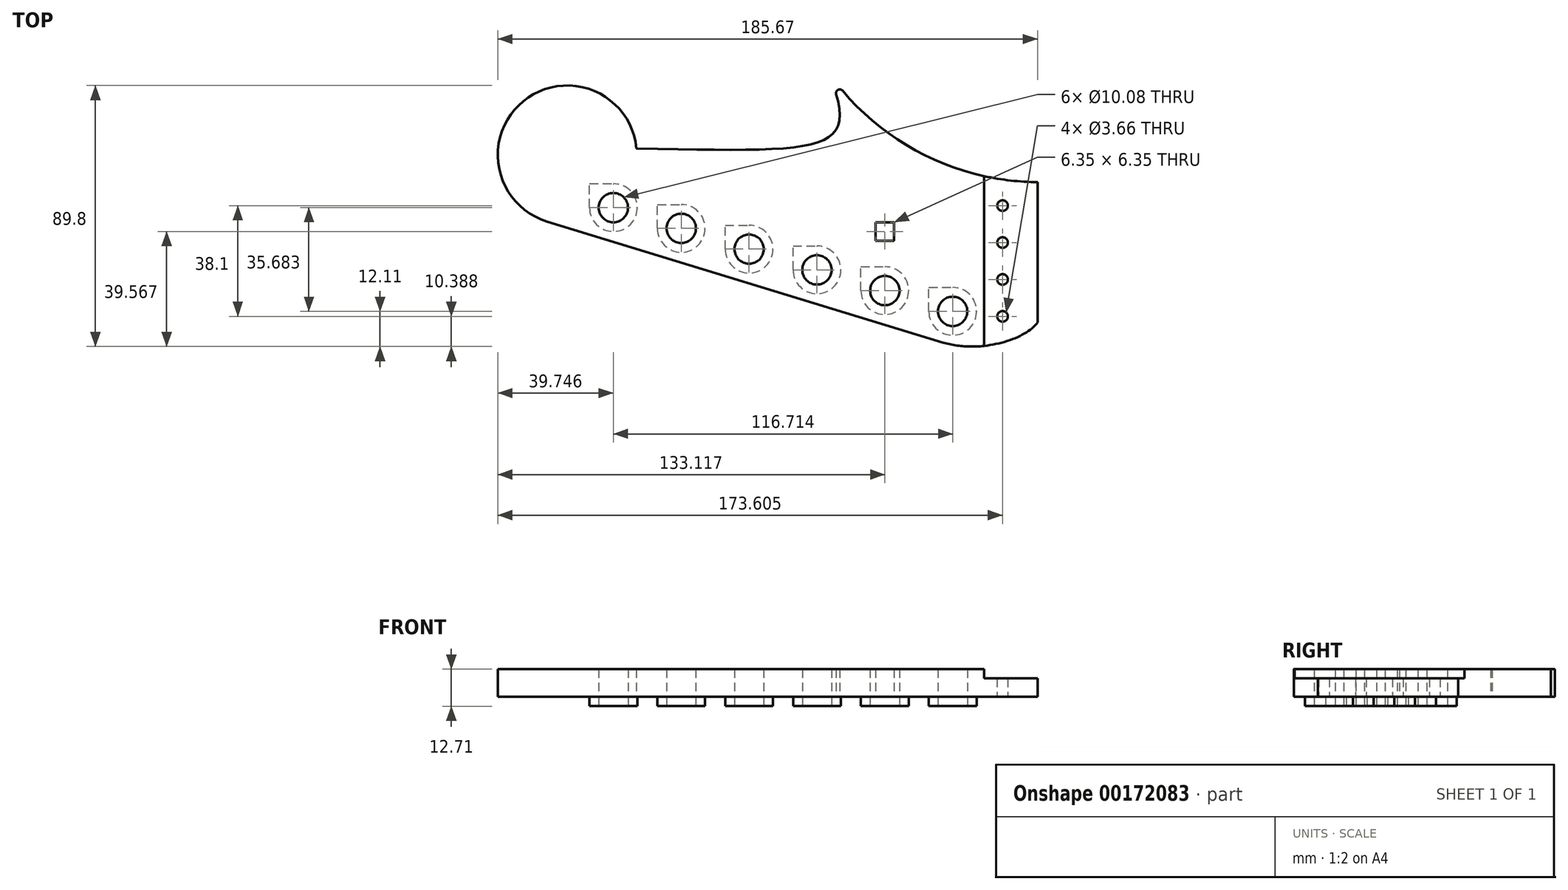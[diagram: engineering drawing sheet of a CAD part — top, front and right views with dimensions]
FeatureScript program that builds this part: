
annotation { "Feature Type Name" : "Feature", "Feature Type Description" : "" }
export const myFeature = defineFeature(function(context is Context, id is Id, definition is map)
    precondition{}
    {
        {
            var Q0;
            Q0=qCreatedBy(makeId("Top.planeOp"),FACE);
            var sketch = newSketch(context, id + "F0", { "sketchPlane" : qUnion([Q0])});
            skPoint(sketch, "E0", {"position": v(-185.67, 33.46) * mm});
            skLineSegment(sketch, "E1", {"start": v(0, 24.13) * mm, "end": v(0, -24.13) * mm});
            skCircle(sketch, "E2", {"center": v(-29.21, -20.32) * mm, "radius": 5.04 * mm});
            skLineSegment(sketch, "E3", {"start": v(0, 0) * mm, "end": v(0, 0) * mm});
            skPoint(sketch, "E3.endSnap0", {"position": v(0, 0) * mm});
            skCircle(sketch, "E4.1.0.0", {"center": v(-52.55, -13.18) * mm, "radius": 5.04 * mm});
            skCircle(sketch, "E4.2.0.0", {"center": v(-75.9, -6.05) * mm, "radius": 5.04 * mm});
            skCircle(sketch, "E4.3.0.0", {"center": v(-99.24, 1.09) * mm, "radius": 5.04 * mm});
            skCircle(sketch, "E4.4.0.0", {"center": v(-122.58, 8.23) * mm, "radius": 5.04 * mm});
            skCircle(sketch, "E4.5.0.0", {"center": v(-145.92, 15.36) * mm, "radius": 5.04 * mm});
            skLineSegment(sketch, "E4.direction1", {"start": v(-29.21, -20.32) * mm, "end": v(-52.55, -13.18) * mm, "construction": true});
            skLineSegment(sketch, "E5", {"start": v(-18.42, 26.22) * mm, "end": v(-18.41, -32.2) * mm});
            skLineSegment(sketch, "E6", {"start": v(-32.5, -31.06) * mm, "end": v(-168.76, 10.6) * mm});
            skLineSegment(sketch, "E7", {"start": v(-29.21, -20.32) * mm, "end": v(-32.5, -31.06) * mm, "construction": true});
            skFitSpline(sketch, "E8", {"points": [v(-32.5, -31.06) * mm, v(0, -24.13) * mm], "startDerivative": vector(36.44, -11.14) * mm, "endDerivative": vector(14.29, 19.05) * mm});
            skLineSegment(sketch, "E9", {"start": v(0, 0) * mm, "end": v(99.12, 0) * mm, "construction": true});
            skArc(sketch, "E10", {"start": v(-168.76, 10.6) * mm, "mid": v(-180.99, 19.25) * mm, "end": v(-185.67, 33.46) * mm});
            skLineSegment(sketch, "E11", {"start": v(-185.67, 33.46) * mm, "end": v(-185.67, 61.73) * mm, "construction": true});
            skArc(sketch, "E12", {"start": v(-137.98, 35.75) * mm, "mid": v(-162.91, 57.34) * mm, "end": v(-185.67, 33.46) * mm});
            skArc(sketch, "E13", {"start": v(-72.27, 62.33) * mm, "mid": v(-40.79, 34.43) * mm, "end": v(0, 24.13) * mm});
            skLineSegment(sketch, "E14", {"start": v(8.57, 3.57) * mm, "end": v(-99.24, 3.57) * mm, "construction": true});
            skLineSegment(sketch, "E15", {"start": v(8.57, -3.57) * mm, "end": v(-75.9, -3.57) * mm, "construction": true});
            skCircle(sketch, "E16", {"center": v(-75.9, -6.05) * mm, "radius": 2.48 * mm});
            skCircle(sketch, "E17", {"center": v(-99.24, 1.09) * mm, "radius": 2.48 * mm});
            skLineSegment(sketch, "E18", {"start": v(-99.24, 3.57) * mm, "end": v(-99.24, 1.09) * mm, "construction": true});
            skLineSegment(sketch, "E19", {"start": v(-75.9, -3.57) * mm, "end": v(-75.9, -6.05) * mm, "construction": true});
            skLineSegment(sketch, "E20", {"start": v(-137.98, 35.75) * mm, "end": v(-72.27, 62.33) * mm, "construction": true});
            skFitSpline(sketch, "E21", {"points": [v(-137.98, 35.75) * mm, v(-72.27, 62.33) * mm], "startDerivative": vector(194.61, -3.65) * mm, "endDerivative": vector(-37.72, 87.36) * mm});
            skCircle(sketch, "E22", {"center": v(-122.58, 8.23) * mm, "radius": 2.48 * mm});
            skCircle(sketch, "E23", {"center": v(-145.92, 15.36) * mm, "radius": 2.48 * mm});
            skLineSegment(sketch, "E24", {"start": v(-122.58, 8.23) * mm, "end": v(-122.58, 10.7) * mm});
            skLineSegment(sketch, "E25", {"start": v(-145.92, 15.36) * mm, "end": v(-145.92, 17.84) * mm});
            skLineSegment(sketch, "E26", {"start": v(-122.58, 10.7) * mm, "end": v(7.67, 10.7) * mm, "construction": true});
            skLineSegment(sketch, "E27", {"start": v(-145.92, 17.84) * mm, "end": v(21.7, 17.84) * mm, "construction": true});
            skSolve(sketch);
        }
        {
            var Q0;
            Q0=qSketchRegion(id+"F0",true);
            extrude(context, id + "F1", {"entities" : qUnion([Q0]), "depth" : 6.35 * mm});
        }
        {
            var Q0;
            Q0=makeQuery(id+"F0.imprint","IMPRINT",FACE,{"disambiguationData":[TD([[makeQuery(id+"F0.imprint","IMPRINT",EDGE,{"derivedFrom":sQuery(id+"F0.wireOp",EDGE,"E2")}),-1.0]])]});
            extrude(context, id + "F2", {"entities" : qUnion([Q0]), "operationType" : NewBodyOperationType.ADD, "depth" : 9.52 * mm});
        }
        {
            var Q0;
            Q0=makeQuery(id+"F1.opExtrude","CAP_FACE",FACE,{"disambiguationData":[OSD([sQuery(id+"F0.wireOp",EDGE,"4aa001a9-7916-4ac9-b611-f33505b9f3c5"),sQuery(id+"F0.wireOp",EDGE,"77602153-f705-4483-a7fc-31cc86b3ea61"),sQuery(id+"F0.wireOp",EDGE,"ee52411e-a9e7-4ef9-bd5f-1803b2297118"),sQuery(id+"F0.wireOp",EDGE,"E1"),sQuery(id+"F0.wireOp",EDGE,"E2"),sQuery(id+"F0.wireOp",EDGE,"E4.1.0.0"),sQuery(id+"F0.wireOp",EDGE,"E4.2.0.0"),sQuery(id+"F0.wireOp",EDGE,"E4.3.0.0"),sQuery(id+"F0.wireOp",EDGE,"E4.4.0.0"),sQuery(id+"F0.wireOp",EDGE,"E4.5.0.0"),sQuery(id+"F0.wireOp",EDGE,"05dfdfb5-9140-4733-bf36-b7656169c247"),sQuery(id+"F0.wireOp",EDGE,"fa98ec53-b239-455b-819f-4d27d42f24a3")])],"isStart":false});
            var sketch = newSketch(context, id + "F3", { "sketchPlane" : qUnion([Q0])});
            skPoint(sketch, "E28", {"position": v(-12.06, -22.04) * mm});
            skPoint(sketch, "E29", {"position": v(-12.06, 16.06) * mm});
            skPoint(sketch, "E30", {"position": v(-12.07, 3.36) * mm});
            skPoint(sketch, "E31", {"position": v(-12.06, -9.34) * mm});
            skLineSegment(sketch, "E32", {"start": v(0, -3) * mm, "end": v(-18.41, -3) * mm, "construction": true});
            skSolve(sketch);
        }
        {
            var Q0;
            Q0=sQuery(id+"F3.wireOp",VERTEX,"E29");
            var Q1;
            Q1=sQuery(id+"F3.wireOp",VERTEX,"E30");
            var Q2;
            Q2=sQuery(id+"F3.wireOp",VERTEX,"E31");
            var Q3;
            Q3=sQuery(id+"F3.wireOp",VERTEX,"E28");
            var Q4;
            Q4=makeQuery(id+"F1.opExtrude","SWEPT_BODY",BODY,{"disambiguationData":[OSD([sQuery(id+"F0.wireOp",EDGE,"4aa001a9-7916-4ac9-b611-f33505b9f3c5"),sQuery(id+"F0.wireOp",EDGE,"77602153-f705-4483-a7fc-31cc86b3ea61"),sQuery(id+"F0.wireOp",EDGE,"ee52411e-a9e7-4ef9-bd5f-1803b2297118"),sQuery(id+"F0.wireOp",EDGE,"E1"),sQuery(id+"F0.wireOp",EDGE,"E2"),sQuery(id+"F0.wireOp",EDGE,"E4.1.0.0"),sQuery(id+"F0.wireOp",EDGE,"E4.2.0.0"),sQuery(id+"F0.wireOp",EDGE,"E4.3.0.0"),sQuery(id+"F0.wireOp",EDGE,"E4.4.0.0"),sQuery(id+"F0.wireOp",EDGE,"E4.5.0.0"),sQuery(id+"F0.wireOp",EDGE,"05dfdfb5-9140-4733-bf36-b7656169c247"),sQuery(id+"F0.wireOp",EDGE,"fa98ec53-b239-455b-819f-4d27d42f24a3")])]});
            hole(context, id + "F4", {"style" : HoleStyle.SIMPLE, "endStyle" : HoleEndStyle.THROUGH, "standardTappedOrClearance" : lookupTablePath({ "standard" : "ANSI", "fit" : "Close", "size" : "#6", "type" : "Clearance" }), "standardBlindInLast" : lookupTablePath({ "fit" : "Close", "standard" : "ANSI", "size" : "#6", "type" : "Clearance" }), "holeDiameter" : 3.66 * mm, "locations" : qUnion([Q0, Q1, Q2, Q3]), "scope" : qUnion([Q4]), "isTappedThrough" : true, "startStyle" : HoleStartStyle.SKETCH});
        }
        {
            var Q0;
            {var subQ0=sQuery(id+"F0.wireOp",EDGE,"E21");var subQ1=sQuery(id+"F0.wireOp",EDGE,"E13");Q0=makeQuery(id+"F2.boolean.opBoolean","MERGE",EDGE,{"derivedFrom":[makeQuery(id+"F1.opExtrude","SWEPT_EDGE",EDGE,{"disambiguationData":[OSD([subQ1,subQ0])]}),makeQuery(id+"F2.opExtrude","SWEPT_EDGE",EDGE,{"disambiguationData":[OSD([subQ1,subQ0])]})]});}
            fillet(context, id + "F5", {"entities" : qUnion([Q0]), "radius" : 1.27 * mm, "tangentPropagation" : true, "allowEdgeOverflow" : false});
        }
        {
            var Q0;
            Q0=makeQuery(id+"F2.opExtrude","CAP_FACE",FACE,{"disambiguationData":[OSD([sQuery(id+"F0.wireOp",EDGE,"E2"),sQuery(id+"F0.wireOp",EDGE,"E4.1.0.0"),sQuery(id+"F0.wireOp",EDGE,"E4.2.0.0"),sQuery(id+"F0.wireOp",EDGE,"E4.3.0.0"),sQuery(id+"F0.wireOp",EDGE,"E4.4.0.0"),sQuery(id+"F0.wireOp",EDGE,"E4.5.0.0"),sQuery(id+"F0.wireOp",EDGE,"E5"),sQuery(id+"F0.wireOp",EDGE,"E6"),sQuery(id+"F0.wireOp",EDGE,"E8"),sQuery(id+"F0.wireOp",EDGE,"E10"),sQuery(id+"F0.wireOp",EDGE,"E12"),sQuery(id+"F0.wireOp",EDGE,"E13"),sQuery(id+"F0.wireOp",EDGE,"E21")])],"isStart":false});
            var sketch = newSketch(context, id + "F6", { "sketchPlane" : qUnion([Q0])});
            skArc(sketch, "E33", {"start": v(-176.02, 0) * mm, "mid": v(-95.34, 4.1) * mm, "end": v(-40.97, 63.86) * mm});
            skArc(sketch, "E34.0", {"start": v(-172.8, 9.1) * mm, "mid": v(-99.46, 12.82) * mm, "end": v(-50.05, 67.14) * mm});
            skArc(sketch, "E35", {"start": v(-33.84, 84.78) * mm, "mid": v(-42.65, 23.63) * mm, "end": v(-29.69, -36.76) * mm});
            skArc(sketch, "E36.0", {"start": v(-38.9, 86.46) * mm, "mid": v(-47.98, 23.45) * mm, "end": v(-34.62, -38.79) * mm});
            skArc(sketch, "E37", {"start": v(-118.56, -20.84) * mm, "mid": v(-145.78, 28.3) * mm, "end": v(-199.55, 44.5) * mm});
            skArc(sketch, "E38.0", {"start": v(-108.22, -19.6) * mm, "mid": v(-139.24, 36.4) * mm, "end": v(-200.52, 54.87) * mm});
            skLineSegment(sketch, "E39.0", {"start": v(-32.5, -31.06) * mm, "end": v(-168.76, 10.6) * mm});
            skArc(sketch, "E39.1", {"start": v(-137.98, 35.75) * mm, "mid": v(-176.9, 51.98) * mm, "end": v(-168.76, 10.6) * mm});
            skFitSpline(sketch, "E39.2", {"points": [v(-137.98, 35.75) * mm, v(-73.1, 34.53) * mm, v(-60.64, 33.21) * mm, v(-73.21, 62.33) * mm]});
            skArc(sketch, "E39.3", {"start": v(-67.1, 55.59) * mm, "mid": v(-68.68, 55.88) * mm, "end": v(-69.28, 54.4) * mm});
            skArc(sketch, "E39.4", {"start": v(-67.1, 55.59) * mm, "mid": v(-45.17, 36.9) * mm, "end": v(-18.41, 26.22) * mm});
            skFitSpline(sketch, "E39.5", {"points": [v(-32.5, -31.06) * mm, v(-20.35, -34.77) * mm, v(-4.76, -30.48) * mm, v(0, -24.13) * mm]});
            skLineSegment(sketch, "E39.6", {"start": v(-18.42, 26.22) * mm, "end": v(-18.41, -32.2) * mm});
            skSolve(sketch);
        }
        {
            var Q0;
            Q0=makeQuery(id+"F2.opExtrude","CAP_FACE",FACE,{"disambiguationData":[OSD([sQuery(id+"F0.wireOp",EDGE,"E2"),sQuery(id+"F0.wireOp",EDGE,"E4.1.0.0"),sQuery(id+"F0.wireOp",EDGE,"E4.2.0.0"),sQuery(id+"F0.wireOp",EDGE,"E4.3.0.0"),sQuery(id+"F0.wireOp",EDGE,"E4.4.0.0"),sQuery(id+"F0.wireOp",EDGE,"E4.5.0.0"),sQuery(id+"F0.wireOp",EDGE,"E5"),sQuery(id+"F0.wireOp",EDGE,"E6"),sQuery(id+"F0.wireOp",EDGE,"E8"),sQuery(id+"F0.wireOp",EDGE,"E10"),sQuery(id+"F0.wireOp",EDGE,"E12"),sQuery(id+"F0.wireOp",EDGE,"E13"),sQuery(id+"F0.wireOp",EDGE,"E21")])],"isStart":false});
            var sketch = newSketch(context, id + "F7", { "sketchPlane" : qUnion([Q0])});
            skLineSegment(sketch, "E40", {"start": v(-13.49, 50.46) * mm, "end": v(-120.4, -45.77) * mm});
            skLineSegment(sketch, "E41", {"start": v(-120.4, -45.77) * mm, "end": v(-124.32, -41.42) * mm});
            skLineSegment(sketch, "E42", {"start": v(-124.32, -41.42) * mm, "end": v(-17.2, 55) * mm});
            skLineSegment(sketch, "E43", {"start": v(-17.2, 55) * mm, "end": v(-13.49, 50.46) * mm});
            skLineSegment(sketch, "E44", {"start": v(-49.09, -54.74) * mm, "end": v(-69.94, 75.3) * mm});
            skLineSegment(sketch, "E45", {"start": v(-69.94, 75.3) * mm, "end": v(-75.5, 74.4) * mm});
            skLineSegment(sketch, "E46", {"start": v(-75.5, 74.4) * mm, "end": v(-54.41, -57.09) * mm});
            skLineSegment(sketch, "E47", {"start": v(-54.41, -57.09) * mm, "end": v(-49.09, -54.74) * mm});
            skLineSegment(sketch, "E48", {"start": v(-151.73, -17.56) * mm, "end": v(37.22, 6.84) * mm});
            skLineSegment(sketch, "E49", {"start": v(37.22, 6.84) * mm, "end": v(35.94, 14.83) * mm});
            skLineSegment(sketch, "E50", {"start": v(35.94, 14.83) * mm, "end": v(-152.1, -9.45) * mm});
            skLineSegment(sketch, "E51", {"start": v(-152.1, -9.45) * mm, "end": v(-151.73, -17.56) * mm});
            skLineSegment(sketch, "E52", {"start": v(-167.26, 91.8) * mm, "end": v(-135.04, -31.2) * mm});
            skLineSegment(sketch, "E53", {"start": v(-135.04, -31.2) * mm, "end": v(-143.78, -33.49) * mm});
            skLineSegment(sketch, "E54", {"start": v(-143.78, -33.49) * mm, "end": v(-175.54, 87.77) * mm});
            skLineSegment(sketch, "E55", {"start": v(-175.54, 87.77) * mm, "end": v(-167.26, 91.8) * mm});
            skLineSegment(sketch, "E56", {"start": v(-107.47, 85.6) * mm, "end": v(-120.17, 6.32) * mm});
            skLineSegment(sketch, "E57", {"start": v(-120.17, 6.32) * mm, "end": v(-125.36, 7.15) * mm});
            skLineSegment(sketch, "E58", {"start": v(-125.36, 7.15) * mm, "end": v(-112.55, 87.16) * mm});
            skLineSegment(sketch, "E59", {"start": v(-112.55, 87.16) * mm, "end": v(-107.47, 85.6) * mm});
            skLineSegment(sketch, "E60", {"start": v(-28.5, -37.42) * mm, "end": v(-138.14, 44.12) * mm});
            skLineSegment(sketch, "E61", {"start": v(-138.14, 44.12) * mm, "end": v(-135.1, 48.2) * mm});
            skLineSegment(sketch, "E62", {"start": v(-135.1, 48.2) * mm, "end": v(-25, -33.69) * mm});
            skLineSegment(sketch, "E63", {"start": v(-25, -33.69) * mm, "end": v(-28.5, -37.42) * mm});
            skLineSegment(sketch, "E64", {"start": v(-38.7, 46.06) * mm, "end": v(-209.58, 10.9) * mm});
            skLineSegment(sketch, "E65", {"start": v(-209.58, 10.9) * mm, "end": v(-211.15, 18.56) * mm});
            skLineSegment(sketch, "E66", {"start": v(-211.15, 18.56) * mm, "end": v(-40.21, 53.74) * mm});
            skLineSegment(sketch, "E67", {"start": v(-40.21, 53.74) * mm, "end": v(-38.7, 46.06) * mm});
            skText(sketch, "E68", { "text": "Bernstein", "fontName": "NotoSerif-Italic.ttf"});
            const initialGuessF7  = {"E68": [-0.0729, 0.03836, -0.97948, -0.20155, 0.00547]};
            skSetInitialGuess(sketch, initialGuessF7);
            skSolve(sketch);
        }
        {
            var Q0;
            Q0=qCreatedBy(makeId("Top.planeOp"),FACE);
            var sketch = newSketch(context, id + "F8", { "sketchPlane" : qUnion([Q0])});
            skLineSegment(sketch, "E69.0", {"start": v(-122.58, 10.7) * mm, "end": v(7.67, 10.7) * mm, "construction": true});
            skLineSegment(sketch, "E69.1", {"start": v(-145.92, 17.84) * mm, "end": v(21.7, 17.84) * mm, "construction": true});
            skLineSegment(sketch, "E70.bottom", {"start": v(-49.38, 3.96) * mm, "end": v(-55.73, 3.96) * mm});
            skLineSegment(sketch, "E70.top", {"start": v(-49.38, 10.31) * mm, "end": v(-55.73, 10.31) * mm});
            skLineSegment(sketch, "E70.left", {"start": v(-49.38, 3.96) * mm, "end": v(-49.38, 10.31) * mm});
            skLineSegment(sketch, "E70.right", {"start": v(-55.73, 3.96) * mm, "end": v(-55.73, 10.31) * mm});
            skPoint(sketch, "E70.middle", {"position": v(-52.55, 7.14) * mm});
            skLineSegment(sketch, "E71.0", {"start": v(8.57, 3.57) * mm, "end": v(-99.24, 3.57) * mm, "construction": true});
            skLineSegment(sketch, "E72", {"start": v(-52.55, 7.14) * mm, "end": v(-66.43, 7.14) * mm, "construction": true});
            skPoint(sketch, "E73", {"position": v(-52.55, -13.18) * mm});
            skSolve(sketch);
        }
        {
            var Q0;
            Q0 = qSketchRegion(id + "F8", true);
            extrude(context, id + "F9", {"entities" : qUnion([Q0]), "operationType" : NewBodyOperationType.REMOVE, "endBound" : BoundingType.THROUGH_ALL, "depth" : 25.4 * mm});
        }
        {
            var Q0;
            Q0=makeQuery(id+"F1.opExtrude","CAP_FACE",FACE,{"disambiguationData":[OSD([sQuery(id+"F0.wireOp",EDGE,"E1"),sQuery(id+"F0.wireOp",EDGE,"E2"),sQuery(id+"F0.wireOp",EDGE,"E4.1.0.0"),sQuery(id+"F0.wireOp",EDGE,"E4.2.0.0"),sQuery(id+"F0.wireOp",EDGE,"E4.3.0.0"),sQuery(id+"F0.wireOp",EDGE,"E4.4.0.0"),sQuery(id+"F0.wireOp",EDGE,"E4.5.0.0"),sQuery(id+"F0.wireOp",EDGE,"E6"),sQuery(id+"F0.wireOp",EDGE,"E8"),sQuery(id+"F0.wireOp",EDGE,"E10"),sQuery(id+"F0.wireOp",EDGE,"E12"),sQuery(id+"F0.wireOp",EDGE,"E13"),sQuery(id+"F0.wireOp",EDGE,"E21")])],"isStart":true});
            var sketch = newSketch(context, id + "F10", { "sketchPlane" : qUnion([Q0])});
            skCircle(sketch, "E74.0", {"center": v(-29.21, 20.32) * mm, "radius": 5.04 * mm});
            skCircle(sketch, "E75.0", {"center": v(-29.21, 20.32) * mm, "radius": 8.22 * mm});
            skLineSegment(sketch, "E76", {"start": v(-37.43, 20.32) * mm, "end": v(-37.43, 12.1) * mm});
            skLineSegment(sketch, "E77", {"start": v(-37.43, 12.1) * mm, "end": v(-29.21, 12.1) * mm});
            skLineSegment(sketch, "E78", {"start": v(-29.2, 20.32) * mm, "end": v(-52.55, 13.18) * mm, "construction": true});
            skLineSegment(sketch, "E79.1.0.0", {"start": v(-60.77, 13.18) * mm, "end": v(-60.77, 4.97) * mm});
            skLineSegment(sketch, "E79.1.0.1", {"start": v(-60.77, 4.97) * mm, "end": v(-52.55, 4.97) * mm});
            skCircle(sketch, "E79.1.0.2", {"center": v(-52.55, 13.18) * mm, "radius": 8.22 * mm});
            skCircle(sketch, "E79.1.0.3", {"center": v(-52.55, 13.18) * mm, "radius": 5.04 * mm});
            skLineSegment(sketch, "E79.2.0.0", {"start": v(-84.11, 6.05) * mm, "end": v(-84.11, -2.17) * mm});
            skLineSegment(sketch, "E79.2.0.1", {"start": v(-84.11, -2.17) * mm, "end": v(-75.9, -2.17) * mm});
            skCircle(sketch, "E79.2.0.2", {"center": v(-75.9, 6.05) * mm, "radius": 8.22 * mm});
            skCircle(sketch, "E79.2.0.3", {"center": v(-75.9, 6.05) * mm, "radius": 5.04 * mm});
            skLineSegment(sketch, "E79.3.0.0", {"start": v(-107.46, -1.09) * mm, "end": v(-107.46, -9.3) * mm});
            skLineSegment(sketch, "E79.3.0.1", {"start": v(-107.46, -9.3) * mm, "end": v(-99.24, -9.3) * mm});
            skCircle(sketch, "E79.3.0.2", {"center": v(-99.24, -1.09) * mm, "radius": 8.22 * mm});
            skCircle(sketch, "E79.3.0.3", {"center": v(-99.24, -1.09) * mm, "radius": 5.04 * mm});
            skLineSegment(sketch, "E79.4.0.0", {"start": v(-130.8, -8.23) * mm, "end": v(-130.8, -16.44) * mm});
            skLineSegment(sketch, "E79.4.0.1", {"start": v(-130.8, -16.44) * mm, "end": v(-122.58, -16.44) * mm});
            skCircle(sketch, "E79.4.0.2", {"center": v(-122.58, -8.23) * mm, "radius": 8.22 * mm});
            skCircle(sketch, "E79.4.0.3", {"center": v(-122.58, -8.23) * mm, "radius": 5.04 * mm});
            skLineSegment(sketch, "E79.5.0.0", {"start": v(-154.14, -15.36) * mm, "end": v(-154.14, -23.58) * mm});
            skLineSegment(sketch, "E79.5.0.1", {"start": v(-154.14, -23.58) * mm, "end": v(-145.92, -23.58) * mm});
            skCircle(sketch, "E79.5.0.2", {"center": v(-145.92, -15.36) * mm, "radius": 8.22 * mm});
            skCircle(sketch, "E79.5.0.3", {"center": v(-145.92, -15.36) * mm, "radius": 5.04 * mm});
            skSolve(sketch);
        }
        {
            var Q0;
            Q0 = qSketchRegion(id + "F10", true);
            extrude(context, id + "F11", {"entities" : qUnion([Q0]), "operationType" : NewBodyOperationType.ADD, "depth" : 3.17 * mm});
        }
    });
